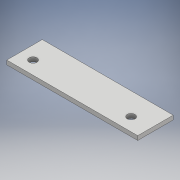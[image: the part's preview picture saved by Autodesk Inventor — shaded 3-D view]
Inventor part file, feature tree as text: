
AUTODESK INVENTOR PART (.ipt)
format: ipt  version: 2018.3 (Build 223284000, 284)  size: 99,840 bytes
history: native  units: mm
features: extrude x1, sketch x1
ambient origin geometry x8: Origin, YZ Plane, XZ Plane, XY Plane, X Axis, Y Axis, Z Axis, Center Point
bodies: Solid1 (feature_tree)
feature tree (2):
  extrude  "Extrusion1"  Depth=10.0mm
  sketch  "Sketch1"  dims[d0=6.0mm d1=10.0mm d2=10.0mm d3=6.0mm d4=74.71mm d5=15.0mm d6=3.175mm d7=0.0mm]
